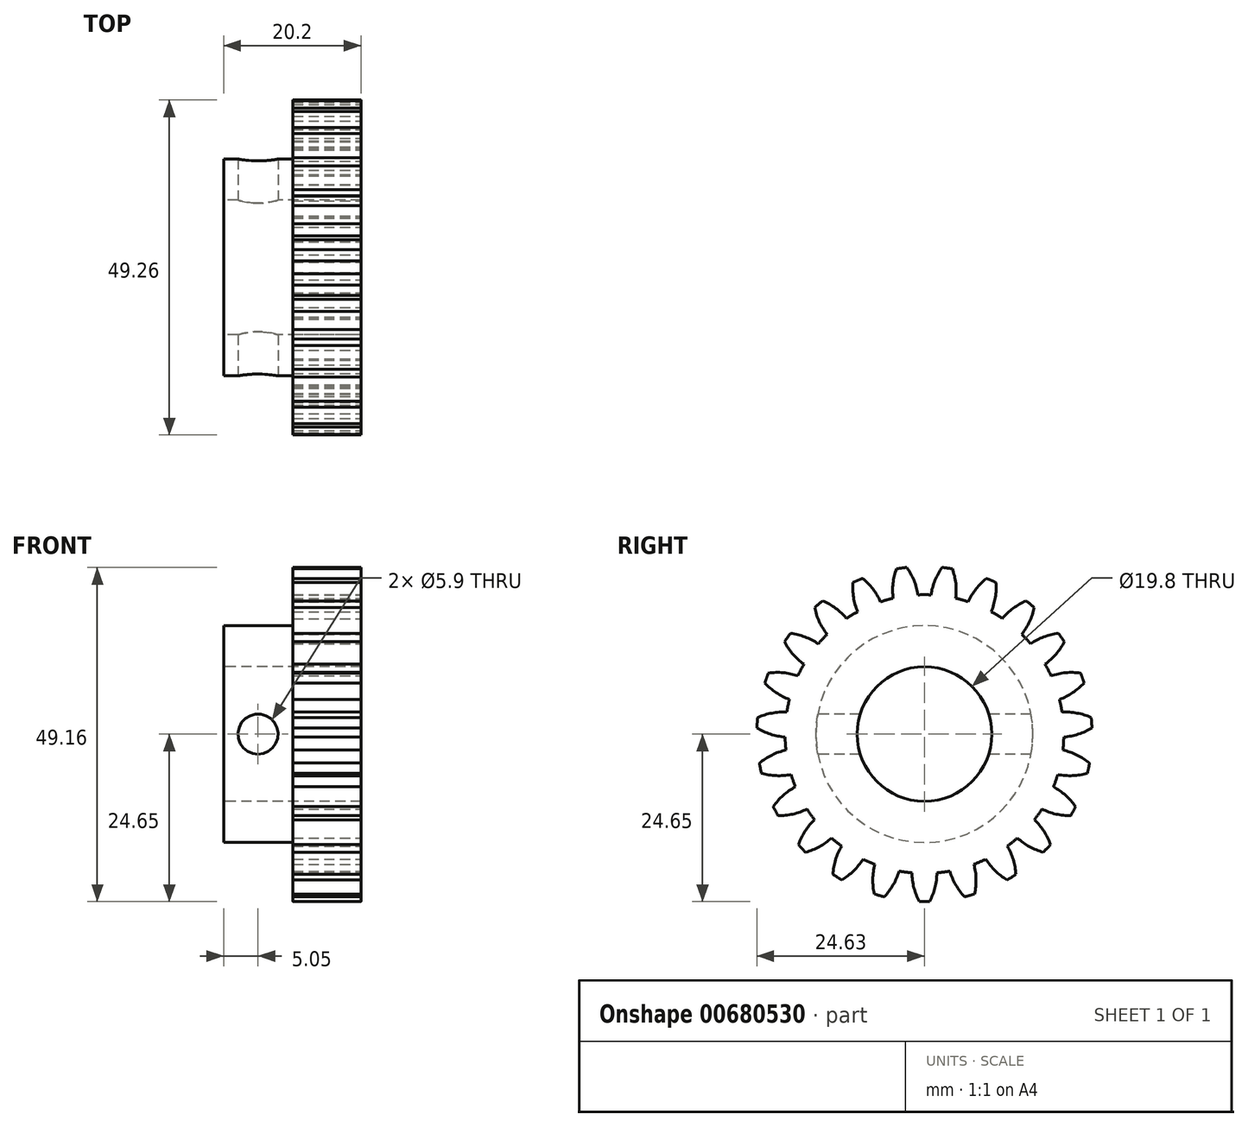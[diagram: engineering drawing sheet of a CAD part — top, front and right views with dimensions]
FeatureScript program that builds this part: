
annotation { "Feature Type Name" : "Feature", "Feature Type Description" : "" }
export const myFeature = defineFeature(function(context is Context, id is Id, definition is map)
    precondition{}
    {
        {
            var Q0;
            Q0=qCreatedBy(makeId("Front.planeOp"),FACE);
            var sketch = newSketch(context, id + "F0", { "sketchPlane" : qUnion([Q0])});
            skLineSegment(sketch, "E0", {"start": v(0, 0) * mm, "end": v(0, 15.95) * mm});
            skLineSegment(sketch, "E1", {"start": v(0, 15.95) * mm, "end": v(10.2, 15.95) * mm});
            skLineSegment(sketch, "E2", {"start": v(10.2, 15.95) * mm, "end": v(10.2, 24.65) * mm});
            skLineSegment(sketch, "E3", {"start": v(10.2, 24.65) * mm, "end": v(20.2, 24.65) * mm});
            skLineSegment(sketch, "E4", {"start": v(20.2, 24.65) * mm, "end": v(20.2, 0) * mm});
            skLineSegment(sketch, "E5", {"start": v(20.2, 0) * mm, "end": v(0, 0) * mm});
            skSolve(sketch);
        }
        {
            var Q0;
            Q0=makeQuery(id+"F0.imprint","IMPRINT",FACE,{"disambiguationData":[TD([[makeQuery(id+"F0.imprint","IMPRINT",EDGE,{"derivedFrom":sQuery(id+"F0.wireOp",EDGE,"E0")}),-1.0]])]});
            var Q1;
            Q1=sQuery(id+"F0.wireOp",EDGE,"E5");
            revolve(context, id + "F1", {"entities" : qUnion([Q0]), "axis" : qUnion([Q1]), "revolveType" : RevolveType.FULL});
        }
        {
            var Q0;
            Q0=makeQuery(id+"F1.opRevolve","SWEPT_FACE",FACE,{"disambiguationData":[OSD([sQuery(id+"F0.wireOp",EDGE,"E0")])]});
            var sketch = newSketch(context, id + "F2", { "sketchPlane" : qUnion([Q0])});
            skCircle(sketch, "E6", {"center": v(0, 0) * mm, "radius": 9.9 * mm});
            skSolve(sketch);
        }
        {
            var Q0;
            Q0=makeQuery(id+"F2.imprint","IMPRINT",FACE,{"disambiguationData":[TD([[makeQuery(id+"F2.imprint","IMPRINT",EDGE,{"derivedFrom":sQuery(id+"F2.wireOp",EDGE,"E6")}),1.0]])]});
            extrude(context, id + "F3", {"entities" : qUnion([Q0]), "operationType" : NewBodyOperationType.REMOVE, "oppositeDirection" : true, "depth" : 25 * mm, "offsetDistance" : 25 * mm});
        }
        {
            var Q0;
            Q0=makeQuery(id+"F1.opRevolve","SWEPT_FACE",FACE,{"disambiguationData":[OSD([sQuery(id+"F0.wireOp",EDGE,"E4")])]});
            var sketch = newSketch(context, id + "F4", { "sketchPlane" : qUnion([Q0])});
            skCircle(sketch, "E7", {"center": v(0, 0) * mm, "radius": 23 * mm, "construction": true});
            skCircle(sketch, "E8", {"center": v(0, 0) * mm, "radius": 25.03 * mm});
            skCircle(sketch, "E9", {"center": v(0, 0) * mm, "radius": 21.61 * mm, "construction": true});
            skCircle(sketch, "E10", {"center": v(0, 0) * mm, "radius": 20.5 * mm});
            skLineSegment(sketch, "E11", {"start": v(0, 0) * mm, "end": v(-7.83, 56.94) * mm, "construction": true});
            skLineSegment(sketch, "E12", {"start": v(0, 0) * mm, "end": v(0, 56.94) * mm, "construction": true});
            skLineSegment(sketch, "E13", {"start": v(-6.21, 55.87) * mm, "end": v(-1.69, 22.94) * mm, "construction": true});
            skArc(sketch, "E14", {"start": v(-0.96, 20.48) * mm, "mid": v(-1.62, 22.8) * mm, "end": v(-2.87, 24.86) * mm});
            skArc(sketch, "E15.MirrorCS", {"start": v(0.96, 20.48) * mm, "mid": v(1.62, 22.8) * mm, "end": v(2.87, 24.86) * mm});
            skSolve(sketch);
        }
        {
            var Q0;
            {var subQ0=sQuery(id+"F4.wireOp",EDGE,"E14");var subQ1=sQuery(id+"F4.wireOp",EDGE,"E10");var subQ2=makeQuery(id+"F4.imprint","INTERSECT",VERTEX,{"derivedFrom":[subQ1,subQ0]});Q0=makeQuery(id+"F4.imprint","IMPRINT",FACE,{"disambiguationData":[TD([[makeQuery(id+"F4.imprint","IMPRINT",EDGE,{"disambiguationData":[TD([[subQ2,1.0]])],"derivedFrom":subQ1}),-1.0]])]});}
            var Q1;
            {var subQ0=sQuery(id+"F4.wireOp",EDGE,"E14");var subQ1=sQuery(id+"F4.wireOp",EDGE,"E8");var subQ2=makeQuery(id+"F4.imprint","INTERSECT",VERTEX,{"derivedFrom":[subQ1,subQ0]});Q1=makeQuery(id+"F4.imprint","IMPRINT",FACE,{"disambiguationData":[TD([[makeQuery(id+"F4.imprint","IMPRINT",EDGE,{"disambiguationData":[TD([[subQ2,1.0]])],"derivedFrom":subQ1}),1.0]])]});}
            extrude(context, id + "F5", {"entities" : qUnion([Q0, Q1]), "operationType" : NewBodyOperationType.REMOVE, "oppositeDirection" : true, "depth" : 25 * mm, "offsetDistance" : 25 * mm});
        }
        {
            var Q0;
            Q0=makeQuery(id+"F5.boolean.opBoolean","COPY",FACE,{"derivedFrom":makeQuery(id+"F5.opExtrude","SWEPT_FACE",FACE,{"disambiguationData":[OSD([sQuery(id+"F4.wireOp",EDGE,"E14")])]})});
            var Q1;
            Q1=makeQuery(id+"F5.boolean.opBoolean","COPY",FACE,{"derivedFrom":makeQuery(id+"F5.opExtrude","SWEPT_FACE",FACE,{"disambiguationData":[OSD([sQuery(id+"F4.wireOp",EDGE,"E10")])]})});
            var Q2;
            Q2=makeQuery(id+"F5.boolean.opBoolean","COPY",FACE,{"derivedFrom":makeQuery(id+"F5.opExtrude","SWEPT_FACE",FACE,{"disambiguationData":[OSD([sQuery(id+"F4.wireOp",EDGE,"E15.MirrorCS")])]})});
            var Q3;
            Q3=makeQuery(id+"F1.opRevolve","SWEPT_FACE",FACE,{"disambiguationData":[OSD([sQuery(id+"F0.wireOp",EDGE,"E3")])]});
            circularPattern(context, id + "F6", {"patternType" : PatternType.FACE, "faces" : qUnion([Q0, Q1, Q2]), "axis" : qUnion([Q3]), "angle" : 360 * degree, "instanceCount" : 23, "equalSpace" : true});
        }
        {
            var Q0;
            Q0=qCreatedBy(makeId("Front.planeOp"),FACE);
            var sketch = newSketch(context, id + "F7", { "sketchPlane" : qUnion([Q0])});
            skCircle(sketch, "E16", {"center": v(5.05, 0) * mm, "radius": 2.95 * mm});
            skSolve(sketch);
        }
        {
            var Q0;
            Q0 = qSketchRegion(id + "F7", true);
            extrude(context, id + "F8", {"entities" : qUnion([Q0]), "operationType" : NewBodyOperationType.REMOVE, "endBound" : BoundingType.SYMMETRIC, "oppositeDirection" : true, "depth" : 49.8 * mm, "offsetDistance" : 25 * mm});
        }
    });
